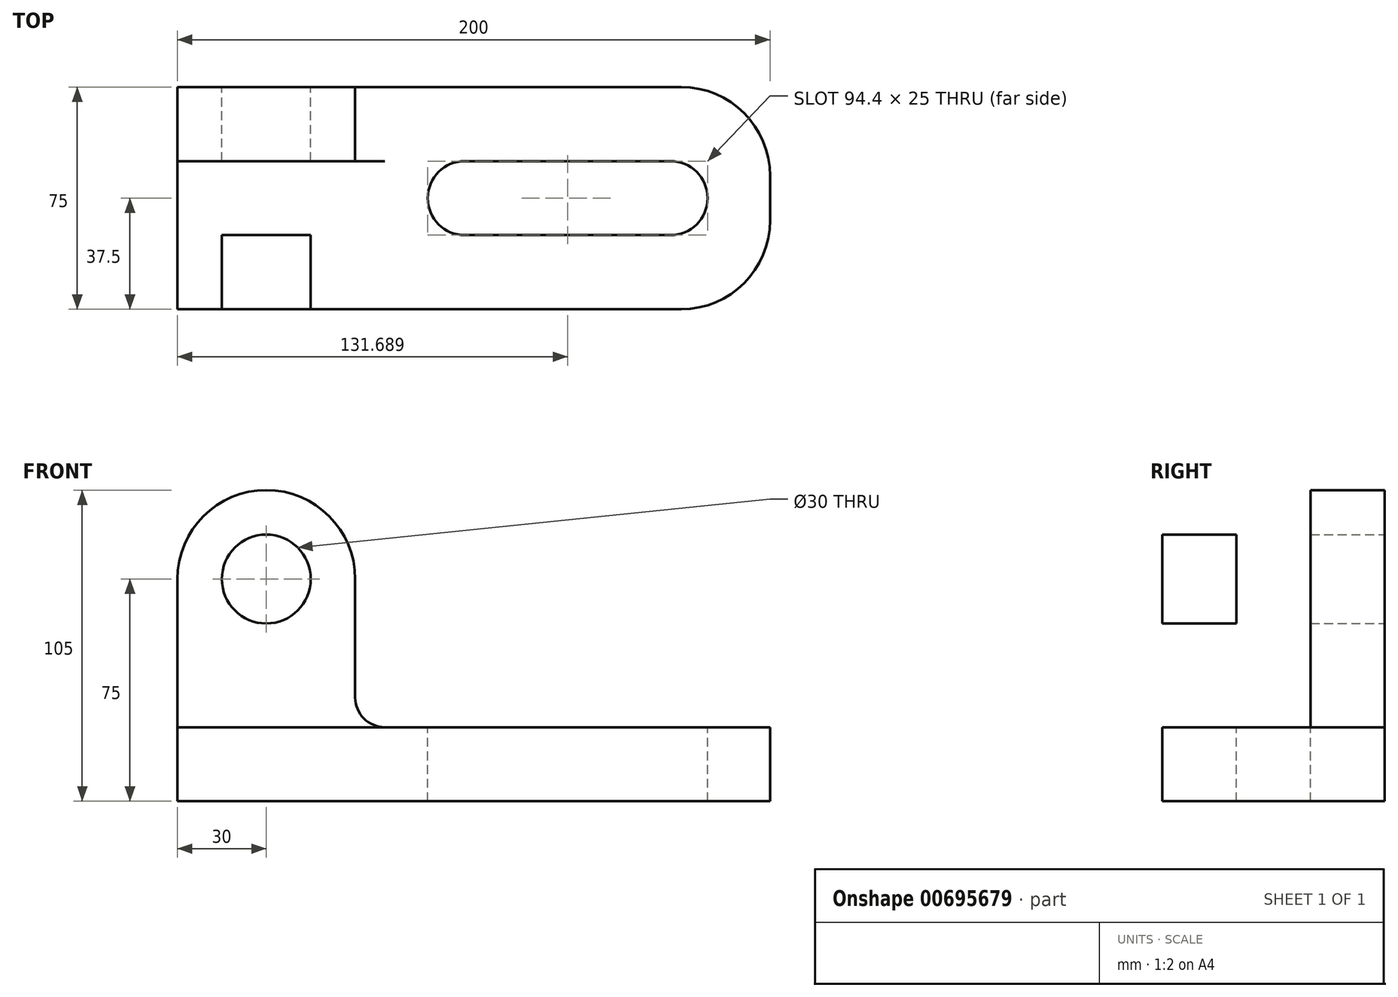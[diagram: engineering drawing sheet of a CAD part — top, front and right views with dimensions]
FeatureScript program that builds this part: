
annotation { "Feature Type Name" : "Feature", "Feature Type Description" : "" }
export const myFeature = defineFeature(function(context is Context, id is Id, definition is map)
    precondition{}
    {
        {
            var Q0;
            Q0=qCreatedBy(makeId("Front.planeOp"),FACE);
            var sketch = newSketch(context, id + "F0", { "sketchPlane" : qUnion([Q0])});
            skCircle(sketch, "E0", {"center": v(0, 0) * mm, "radius": 15 * mm});
            skArc(sketch, "E1", {"start": v(30, 0) * mm, "mid": v(0, 30) * mm, "end": v(-30, 0) * mm});
            skLineSegment(sketch, "E2", {"start": v(-30, 0) * mm, "end": v(-30, -75) * mm});
            skLineSegment(sketch, "E3", {"start": v(-30, -75) * mm, "end": v(170, -75) * mm});
            skLineSegment(sketch, "E4", {"start": v(170, -75) * mm, "end": v(170, -50) * mm});
            skLineSegment(sketch, "E5", {"start": v(30, 0) * mm, "end": v(30, -40) * mm});
            skLineSegment(sketch, "E6", {"start": v(40, -50) * mm, "end": v(170, -50) * mm});
            skPoint(sketch, "E7.visualSharp", {"position": v(30, -50) * mm});
            skArc(sketch, "E7.filletArc", {"start": v(30, -40) * mm, "mid": v(32.93, -47.07) * mm, "end": v(40, -50) * mm});
            skLineSegment(sketch, "E8", {"start": v(40, -50) * mm, "end": v(-30, -50) * mm});
            skSolve(sketch);
        }
        {
            var Q0;
            {var subQ0=sQuery(id+"F0.wireOp",EDGE,"E3");Q0=makeQuery(id+"F0.imprint","IMPRINT",FACE,{"disambiguationData":[TD([[makeQuery(id+"F0.imprint","IMPRINT",EDGE,{"derivedFrom":subQ0}),1.0]])]});}
            extrude(context, id + "F1", {"entities" : qUnion([Q0]), "depth" : 75 * mm, "offsetDistance" : 25 * mm});
        }
        {
            var Q0;
            Q0=makeQuery(id+"F0.imprint","IMPRINT",FACE,{"disambiguationData":[TD([[makeQuery(id+"F0.imprint","IMPRINT",EDGE,{"derivedFrom":sQuery(id+"F0.wireOp",EDGE,"E0")}),-1.0]])]});
            extrude(context, id + "F2", {"entities" : qUnion([Q0]), "operationType" : NewBodyOperationType.ADD, "depth" : 25 * mm, "offsetDistance" : 25 * mm});
        }
        {
            var Q0;
            Q0=makeQuery(id+"F1.opExtrude","CAP_FACE",FACE,{"disambiguationData":[OSD([sQuery(id+"F0.wireOp",EDGE,"E2"),sQuery(id+"F0.wireOp",EDGE,"E3"),sQuery(id+"F0.wireOp",EDGE,"E4"),sQuery(id+"F0.wireOp",EDGE,"E6"),sQuery(id+"F0.wireOp",EDGE,"E8")])],"isStart":false});
            var sketch = newSketch(context, id + "F3", { "sketchPlane" : qUnion([Q0])});
            skCircle(sketch, "E9", {"center": v(0, 0) * mm, "radius": 15 * mm});
            skArc(sketch, "E10", {"start": v(30, 0) * mm, "mid": v(0, 30) * mm, "end": v(-30, 0) * mm});
            skLineSegment(sketch, "E11", {"start": v(-30, 0) * mm, "end": v(-30, -50) * mm});
            skLineSegment(sketch, "E12", {"start": v(-30, -50) * mm, "end": v(30, -50) * mm});
            skLineSegment(sketch, "E13", {"start": v(30, -40) * mm, "end": v(30, 0) * mm});
            skLineSegment(sketch, "E14", {"start": v(40, -50) * mm, "end": v(170, -50) * mm});
            skPoint(sketch, "E15.visualSharp", {"position": v(30, -50) * mm});
            skArc(sketch, "E15.filletArc", {"start": v(30, -40) * mm, "mid": v(32.93, -47.07) * mm, "end": v(40, -50) * mm});
            skSolve(sketch);
        }
        {
            var Q0;
            Q0=makeQuery(id+"F3.imprint","IMPRINT",FACE,{"disambiguationData":[TD([[makeQuery(id+"F3.imprint","IMPRINT",EDGE,{"derivedFrom":sQuery(id+"F3.wireOp",EDGE,"E9")}),1.0]])]});
            extrude(context, id + "F4", {"entities" : qUnion([Q0]), "oppositeDirection" : true, "depth" : 25 * mm, "offsetDistance" : 25 * mm});
        }
        {
            var Q0;
            Q0=makeQuery(id+"F1.opExtrude","SWEPT_FACE",FACE,{"disambiguationData":[OSD([sQuery(id+"F0.wireOp",EDGE,"E6"),sQuery(id+"F0.wireOp",EDGE,"E8")])]});
            var sketch = newSketch(context, id + "F5", { "sketchPlane" : qUnion([Q0])});
            skArc(sketch, "E16", {"start": v(67, -25) * mm, "mid": v(54.5, -37.5) * mm, "end": v(67, -50) * mm});
            skPoint(sketch, "E16.centerSnap0", {"position": v(170, -37.5) * mm});
            skArc(sketch, "E17", {"start": v(136.39, -50) * mm, "mid": v(148.89, -37.5) * mm, "end": v(136.39, -25) * mm});
            skLineSegment(sketch, "E18", {"start": v(67, -25) * mm, "end": v(136.39, -25) * mm});
            skLineSegment(sketch, "E19", {"start": v(67, -50) * mm, "end": v(136.39, -50) * mm});
            skSolve(sketch);
        }
        {
            var Q0;
            Q0 = qSketchRegion(id + "F5", true);
            extrude(context, id + "F6", {"entities" : qUnion([Q0]), "operationType" : NewBodyOperationType.REMOVE, "oppositeDirection" : true, "depth" : 25 * mm, "offsetDistance" : 25 * mm});
        }
        {
            var Q0;
            Q0=makeQuery(id+"F1.opExtrude","CAP_EDGE",EDGE,{"disambiguationData":[OSD([sQuery(id+"F0.wireOp",EDGE,"E4")])],"isStart":false});
            var Q1;
            Q1=makeQuery(id+"F1.opExtrude","CAP_EDGE",EDGE,{"disambiguationData":[OSD([sQuery(id+"F0.wireOp",EDGE,"E4")])],"isStart":true});
            fillet(context, id + "F7", {"entities" : qUnion([Q0, Q1]), "radius" : 30 * mm, "tangentPropagation" : true, "allowEdgeOverflow" : false});
        }
    });
